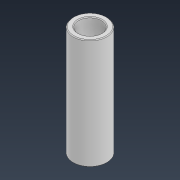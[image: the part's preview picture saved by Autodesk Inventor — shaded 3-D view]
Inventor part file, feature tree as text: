
AUTODESK INVENTOR PART (.ipt)
format: ipt  version: 2022 (Build 260153000, 153)  size: 92,160 bytes
history: native  units: mm
features: extrude x1, chamfer x1, sketch x1
ambient origin geometry x8: Origin, YZ Plane, XZ Plane, XY Plane, X Axis, Y Axis, Z Axis, Center Point
bodies: Solid1 (feature_tree)
feature tree (3):
  extrude  "Extrusion1"  Depth=72.0mm
  chamfer  "Chamfer1"  Distance=72.0mm
  sketch  "Sketch1"  dims[d0=22.0mm d1=15.0mm d2=72.0mm d3=0.0mm d4=0.5mm d5=2.0mm d6=45.0deg]
